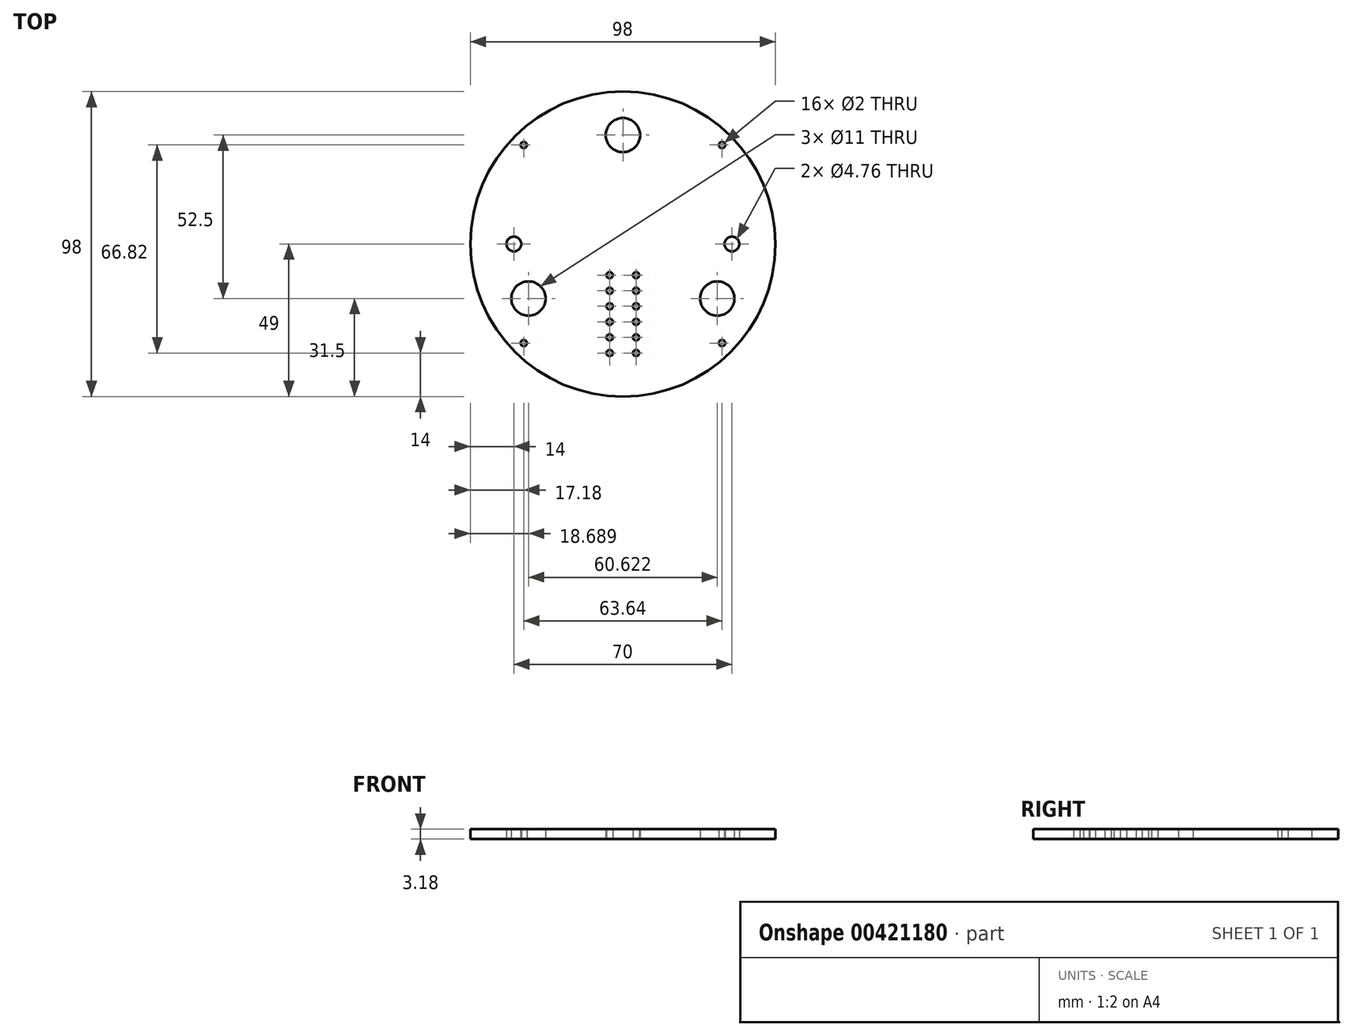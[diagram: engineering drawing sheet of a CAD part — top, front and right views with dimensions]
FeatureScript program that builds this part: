
annotation { "Feature Type Name" : "Feature", "Feature Type Description" : "" }
export const myFeature = defineFeature(function(context is Context, id is Id, definition is map)
    precondition{}
    {
        {
            var Q0;
            Q0=qCreatedBy(makeId("Top.planeOp"),FACE);
            var sketch = newSketch(context, id + "F0", { "sketchPlane" : qUnion([Q0])});
            skCircle(sketch, "E0", {"center": v(0, 0) * mm, "radius": 49 * mm});
            skLineSegment(sketch, "E1", {"start": v(-49, 0) * mm, "end": v(49, 0) * mm});
            skLineSegment(sketch, "E2", {"start": v(0, 0) * mm, "end": v(-35, 0) * mm});
            skCircle(sketch, "E3", {"center": v(-35, 0) * mm, "radius": 2.38 * mm});
            skCircle(sketch, "E4.MirrorC", {"center": v(35, 0) * mm, "radius": 2.38 * mm});
            skCircle(sketch, "E5", {"center": v(-35, 0) * mm, "radius": 7.5 * mm});
            skCircle(sketch, "E6", {"center": v(35, 0) * mm, "radius": 7.5 * mm});
            skLineSegment(sketch, "E7.bottom", {"start": v(25.5, 6) * mm, "end": v(-25.5, 6) * mm});
            skLineSegment(sketch, "E7.top", {"start": v(25.5, 18) * mm, "end": v(-25.5, 18) * mm});
            skLineSegment(sketch, "E7.left", {"start": v(25.5, 6) * mm, "end": v(25.5, 18) * mm});
            skLineSegment(sketch, "E7.right", {"start": v(-25.5, 6) * mm, "end": v(-25.5, 18) * mm});
            skPoint(sketch, "E7.middle", {"position": v(0, 12) * mm});
            skLineSegment(sketch, "E8", {"start": v(0, 0) * mm, "end": v(0, 12) * mm});
            skPoint(sketch, "E9", {"position": v(0, 6) * mm});
            skLineSegment(sketch, "E10", {"start": v(0, 0) * mm, "end": v(0, -10) * mm});
            skLineSegment(sketch, "E11", {"start": v(-4.25, -10) * mm, "end": v(4.25, -10) * mm});
            skLineSegment(sketch, "E12", {"start": v(0, -10) * mm, "end": v(0, -15) * mm});
            skLineSegment(sketch, "E13", {"start": v(-4.25, -10) * mm, "end": v(-4.25, -15) * mm});
            skLineSegment(sketch, "E14", {"start": v(-4.25, -15) * mm, "end": v(-4.25, -20) * mm});
            skLineSegment(sketch, "E15", {"start": v(-4.25, -20) * mm, "end": v(-4.25, -25) * mm});
            skLineSegment(sketch, "E16", {"start": v(-4.25, -25) * mm, "end": v(-4.25, -30) * mm});
            skLineSegment(sketch, "E17", {"start": v(-4.25, -30) * mm, "end": v(-4.25, -35) * mm});
            skLineSegment(sketch, "E18.MirrorCS", {"start": v(4.25, -15) * mm, "end": v(4.25, -20) * mm});
            skLineSegment(sketch, "E19.MirrorCS", {"start": v(4.25, -25) * mm, "end": v(4.25, -30) * mm});
            skLineSegment(sketch, "E20.MirrorCS", {"start": v(4.25, -10) * mm, "end": v(4.25, -15) * mm});
            skLineSegment(sketch, "E21.MirrorCS", {"start": v(4.25, -20) * mm, "end": v(4.25, -25) * mm});
            skLineSegment(sketch, "E22.MirrorCS", {"start": v(4.25, -30) * mm, "end": v(4.25, -35) * mm});
            skCircle(sketch, "E23", {"center": v(-4.25, -35) * mm, "radius": 1 * mm});
            skCircle(sketch, "E24", {"center": v(-4.25, -30) * mm, "radius": 1 * mm});
            skCircle(sketch, "E25", {"center": v(-4.25, -25) * mm, "radius": 1 * mm});
            skCircle(sketch, "E26", {"center": v(-4.25, -20) * mm, "radius": 1 * mm});
            skCircle(sketch, "E27", {"center": v(-4.25, -15) * mm, "radius": 1 * mm});
            skCircle(sketch, "E28", {"center": v(-4.25, -10) * mm, "radius": 1 * mm});
            skCircle(sketch, "E29.MirrorC", {"center": v(4.25, -20) * mm, "radius": 1 * mm});
            skCircle(sketch, "E30.MirrorC", {"center": v(4.25, -10) * mm, "radius": 1 * mm});
            skCircle(sketch, "E31.MirrorC", {"center": v(4.25, -15) * mm, "radius": 1 * mm});
            skCircle(sketch, "E32.MirrorC", {"center": v(4.25, -30) * mm, "radius": 1 * mm});
            skCircle(sketch, "E33.MirrorC", {"center": v(4.25, -25) * mm, "radius": 1 * mm});
            skCircle(sketch, "E34.MirrorC", {"center": v(4.25, -35) * mm, "radius": 1 * mm});
            skLineSegment(sketch, "E35", {"start": v(0, 0) * mm, "end": v(0, 35) * mm});
            skPoint(sketch, "E35.endSnap0", {"position": v(0, 18) * mm});
            skCircle(sketch, "E36", {"center": v(0, 35) * mm, "radius": 5.5 * mm});
            skCircle(sketch, "E37.1.0", {"center": v(-30.31, -17.5) * mm, "radius": 5.5 * mm});
            skCircle(sketch, "E37.2.0", {"center": v(30.31, -17.5) * mm, "radius": 5.5 * mm});
            skLineSegment(sketch, "E38", {"start": v(0, 0) * mm, "end": v(-31.82, -31.82) * mm});
            skCircle(sketch, "E39", {"center": v(-31.82, -31.82) * mm, "radius": 1 * mm});
            skCircle(sketch, "E40.1.0", {"center": v(31.82, -31.82) * mm, "radius": 1 * mm});
            skCircle(sketch, "E40.2.0", {"center": v(31.82, 31.82) * mm, "radius": 1 * mm});
            skCircle(sketch, "E40.3.0", {"center": v(-31.82, 31.82) * mm, "radius": 1 * mm});
            skSolve(sketch);
        }
        {
            var Q0;
            Q0 = qSketchRegion(id + "F0", true);
            var Q1;
            {var subQ0=sQuery(id+"F0.wireOp",EDGE,"E7.right");Q1=makeQuery(id+"F0.imprint","IMPRINT",FACE,{"disambiguationData":[TD([[makeQuery(id+"F0.imprint","IMPRINT",EDGE,{"derivedFrom":subQ0}),-1.0]])]});}
            var Q2;
            {var subQ4=sQuery(id+"F0.wireOp",EDGE,"E7.left");Q2=makeQuery(id+"F0.imprint","IMPRINT",FACE,{"disambiguationData":[TD([[makeQuery(id+"F0.imprint","IMPRINT",EDGE,{"derivedFrom":subQ4}),1.0]])]});}
            var Q3;
            {var subQ0=sQuery(id+"F0.wireOp",EDGE,"E5");var subQ1=sQuery(id+"F0.wireOp",EDGE,"E1");var subQ2=makeQuery(id+"F0.imprint","INTERSECT",VERTEX,{"derivedFrom":[subQ1,subQ0]});Q3=makeQuery(id+"F0.imprint","IMPRINT",FACE,{"disambiguationData":[TD([[makeQuery(id+"F0.imprint","IMPRINT",EDGE,{"disambiguationData":[TD([[subQ2,-1.0]])],"derivedFrom":subQ1}),-1.0]])]});}
            var Q4;
            {var subQ0=sQuery(id+"F0.wireOp",EDGE,"E5");var subQ1=sQuery(id+"F0.wireOp",EDGE,"E1");var subQ2=makeQuery(id+"F0.imprint","INTERSECT",VERTEX,{"derivedFrom":[subQ1,subQ0]});Q4=makeQuery(id+"F0.imprint","IMPRINT",FACE,{"disambiguationData":[TD([[makeQuery(id+"F0.imprint","IMPRINT",EDGE,{"disambiguationData":[TD([[subQ2,-1.0]])],"derivedFrom":subQ1}),1.0]])]});}
            var Q5;
            {var subQ0=sQuery(id+"F0.wireOp",EDGE,"E6");var subQ1=sQuery(id+"F0.wireOp",EDGE,"E1");var subQ2=makeQuery(id+"F0.imprint","INTERSECT",VERTEX,{"disambiguationData":[OD(0.0)],"derivedFrom":[subQ1,subQ0]});Q5=makeQuery(id+"F0.imprint","IMPRINT",FACE,{"disambiguationData":[TD([[makeQuery(id+"F0.imprint","IMPRINT",EDGE,{"disambiguationData":[TD([[subQ2,-1.0]])],"derivedFrom":subQ1}),1.0]])]});}
            var Q6;
            {var subQ0=sQuery(id+"F0.wireOp",EDGE,"E6");var subQ1=sQuery(id+"F0.wireOp",EDGE,"E1");var subQ2=makeQuery(id+"F0.imprint","INTERSECT",VERTEX,{"disambiguationData":[OD(0.0)],"derivedFrom":[subQ1,subQ0]});Q6=makeQuery(id+"F0.imprint","IMPRINT",FACE,{"disambiguationData":[TD([[makeQuery(id+"F0.imprint","IMPRINT",EDGE,{"disambiguationData":[TD([[subQ2,-1.0]])],"derivedFrom":subQ1}),-1.0]])]});}
            extrude(context, id + "F1", {"entities" : qUnion([Q0, Q1, Q2, Q3, Q4, Q5, Q6]), "depth" : 3.17 * mm});
        }
    });
